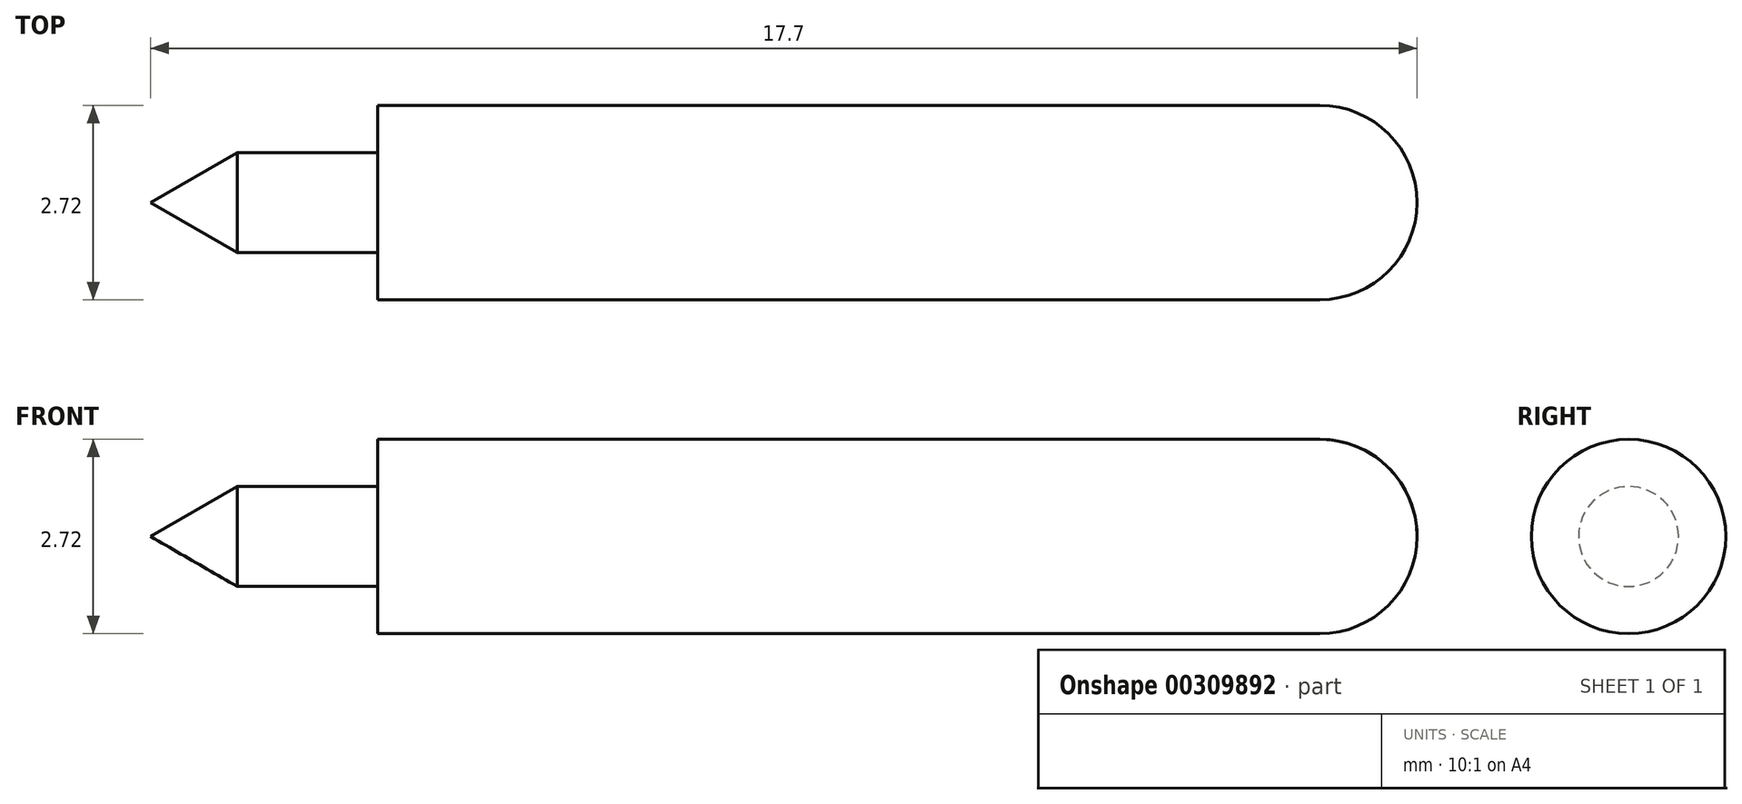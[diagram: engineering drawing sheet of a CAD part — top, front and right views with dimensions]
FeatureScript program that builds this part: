
annotation { "Feature Type Name" : "Feature", "Feature Type Description" : "" }
export const myFeature = defineFeature(function(context is Context, id is Id, definition is map)
    precondition{}
    {
        {
            var Q0;
            Q0=qCreatedBy(makeId("Front.planeOp"),FACE);
            var sketch = newSketch(context, id + "F0", { "sketchPlane" : qUnion([Q0])});
            skLineSegment(sketch, "E0", {"start": v(0, 0) * mm, "end": v(1.2, 0.7) * mm});
            skLineSegment(sketch, "E1", {"start": v(1.2, 0.7) * mm, "end": v(3.17, 0.7) * mm});
            skLineSegment(sketch, "E2", {"start": v(3.18, 0.7) * mm, "end": v(3.18, 1.36) * mm});
            skLineSegment(sketch, "E3", {"start": v(3.17, 1.36) * mm, "end": v(16.34, 1.36) * mm});
            skLineSegment(sketch, "E4", {"start": v(17.7, 0) * mm, "end": v(0, 0) * mm});
            skArc(sketch, "E5", {"start": v(17.7, 0) * mm, "mid": v(17.3, 0.96) * mm, "end": v(16.34, 1.36) * mm});
            skSolve(sketch);
        }
        {
            var Q0;
            Q0=makeQuery(id+"F0.imprint","IMPRINT",FACE,{"disambiguationData":[TD([[makeQuery(id+"F0.imprint","IMPRINT",EDGE,{"derivedFrom":sQuery(id+"F0.wireOp",EDGE,"E0")}),-1.0]])]});
            var Q1;
            Q1=sQuery(id+"F0.wireOp",EDGE,"E4");
            revolve(context, id + "F1", {"entities" : qUnion([Q0]), "axis" : qUnion([Q1]), "revolveType" : RevolveType.FULL});
        }
    });
